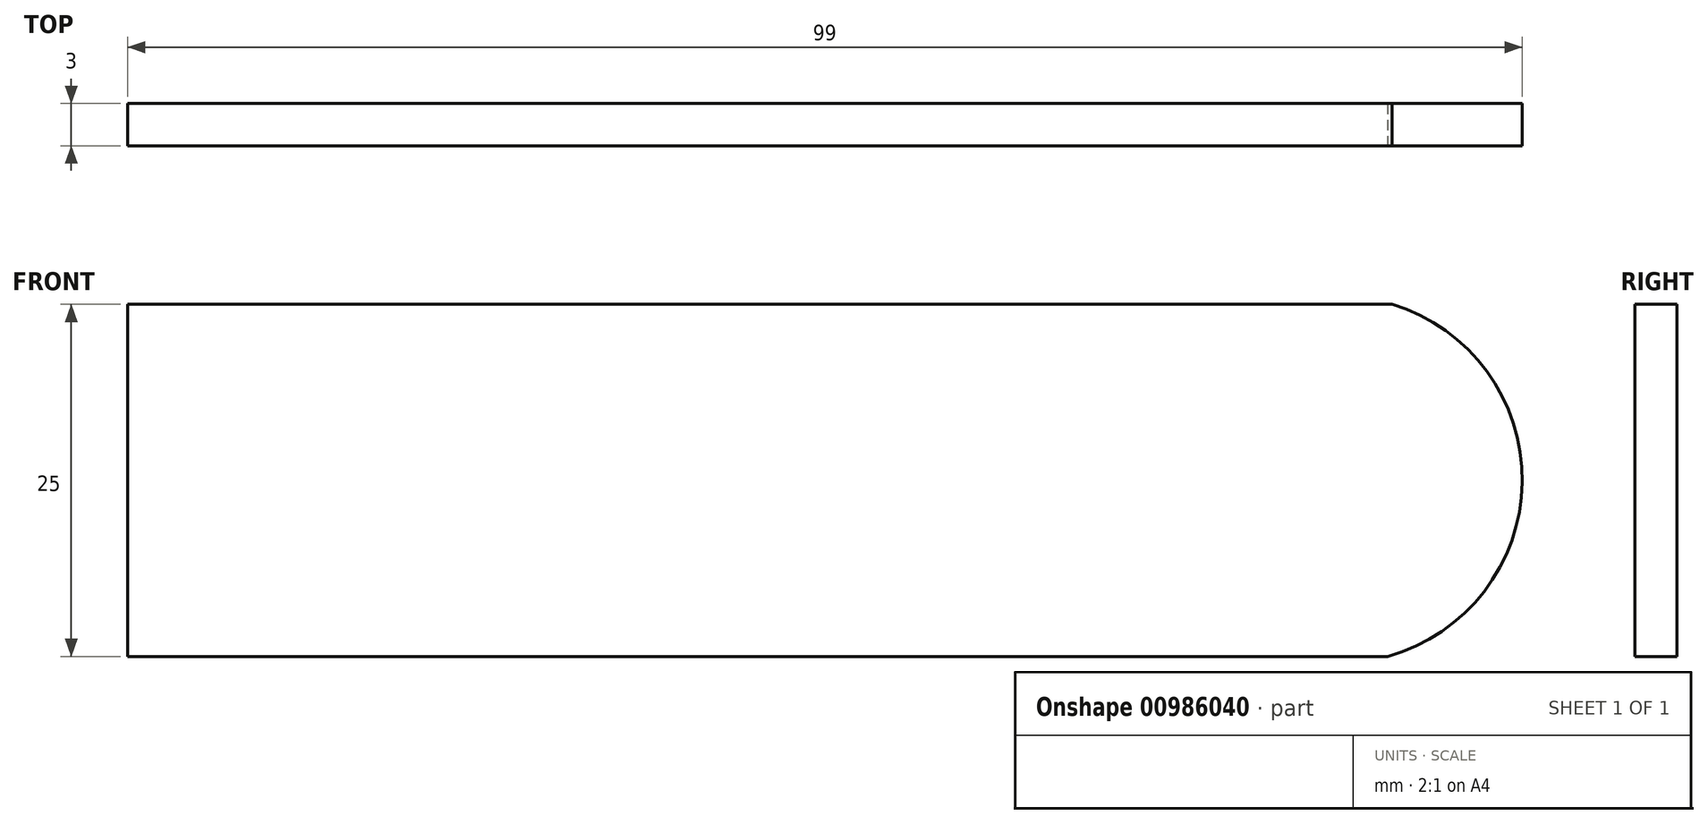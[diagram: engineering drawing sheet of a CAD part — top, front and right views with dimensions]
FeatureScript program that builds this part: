
annotation { "Feature Type Name" : "Feature", "Feature Type Description" : "" }
export const myFeature = defineFeature(function(context is Context, id is Id, definition is map)
    precondition{}
    {
        {
            var Q0;
            Q0=qCreatedBy(makeId("Front.planeOp"),FACE);
            var sketch = newSketch(context, id + "F0", { "sketchPlane" : qUnion([Q0])});
            skLineSegment(sketch, "E0.bottom", {"start": v(0, 0) * mm, "end": v(-100, 0) * mm});
            skLineSegment(sketch, "E0.top", {"start": v(0, 25) * mm, "end": v(-100, 25) * mm});
            skLineSegment(sketch, "E0.left", {"start": v(0, 0) * mm, "end": v(0, 25) * mm});
            skLineSegment(sketch, "E0.right", {"start": v(-100, 0) * mm, "end": v(-100, 25) * mm});
            skSolve(sketch);
        }
        {
            var Q0;
            Q0=makeQuery(id+"F0.imprint","IMPRINT",FACE,{"disambiguationData":[TD([[makeQuery(id+"F0.imprint","IMPRINT",EDGE,{"derivedFrom":sQuery(id+"F0.wireOp",EDGE,"E0.bottom")}),-1.0]])]});
            extrude(context, id + "F1", {"entities" : qUnion([Q0]), "depth" : 3 * mm, "offsetDistance" : 25 * mm});
        }
        {
            var Q0;
            Q0=makeQuery(id+"F1.opExtrude","CAP_FACE",FACE,{"disambiguationData":[OSD([sQuery(id+"F0.wireOp",EDGE,"E0.bottom"),sQuery(id+"F0.wireOp",EDGE,"E0.top"),sQuery(id+"F0.wireOp",EDGE,"E0.left"),sQuery(id+"F0.wireOp",EDGE,"E0.right")])],"isStart":false});
            var sketch = newSketch(context, id + "F2", { "sketchPlane" : qUnion([Q0])});
            skArc(sketch, "E1", {"start": v(-17.49, 0) * mm, "mid": v(-1, 12.71) * mm, "end": v(-17.8, 25) * mm});
            skSolve(sketch);
        }
        {
            var Q0;
            {var subQ5=makeQuery(id+"F1.opExtrude","CAP_EDGE",EDGE,{"disambiguationData":[OSD([sQuery(id+"F0.wireOp",EDGE,"E0.left")])],"isStart":false});Q0=makeQuery(id+"F2.imprint","IMPRINT",FACE,{"disambiguationData":[TD([[makeQuery(id+"F2.imprint","IMPRINT",EDGE,{"derivedFrom":subQ5}),1.0]])]});}
            extrude(context, id + "F3", {"entities" : qUnion([Q0]), "operationType" : NewBodyOperationType.REMOVE, "endBound" : BoundingType.THROUGH_ALL, "oppositeDirection" : true, "depth" : 25 * mm, "offsetDistance" : 25 * mm});
        }
    });
